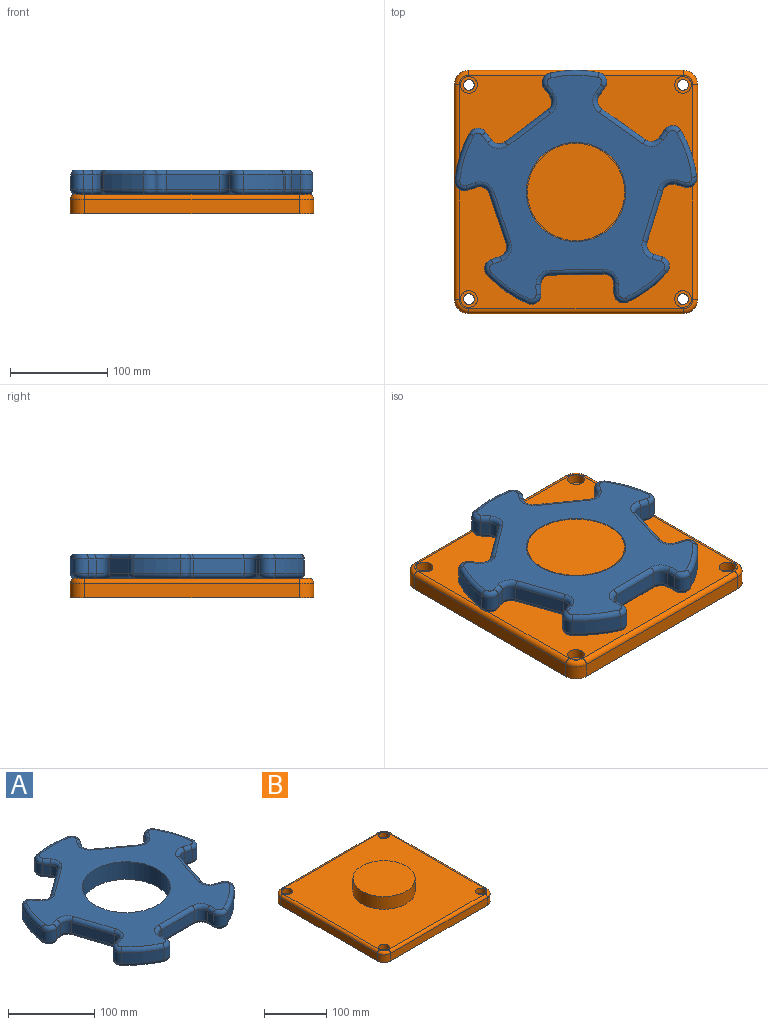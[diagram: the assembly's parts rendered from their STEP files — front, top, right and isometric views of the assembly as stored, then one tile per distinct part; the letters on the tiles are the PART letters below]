
ASSEMBLY  parts=2 mates=1
PART A: 123 faces, bbox 268.9x258.5x25 mm
  f0: plane 238.57x229.73mm, normal (0,0,1), area 21505.7mm2, adj f6,f83,f84,f85,f86,f87,f88,f89
  f1: plane 238.57x229.73mm, normal (0,0,-1), area 21505.7mm2, adj f6,f43,f44,f45,f46,f47,f48,f49
  f2: cylinder r=125mm len=47.82mm, axis (0,0,-1), area 759.5mm2, adj f34,f42,f74,f114
  f3: cylinder r=125mm len=50.29mm, axis (0,0,-1), area 759.5mm2, adj f27,f35,f75,f115
  f4: cylinder r=125mm len=47.82mm, axis (0,0,-1), area 759.5mm2, adj f20,f28,f59,f99
  f5: cylinder r=125mm len=40.68mm, axis (0,0,-1), area 759.5mm2, adj f13,f21,f43,f83
  f6: cylinder r=51mm len=102mm, axis (0,0,-1), area 8011.1mm2, adj f0,f1
  f7: cylinder r=125mm len=40.68mm, axis (0,0,-1), area 759.5mm2, adj f14,f41,f58,f98
  f8: plane 15x9.73mm, normal (-1,0,0), area 146mm2, adj f11,f14,f54,f94
  f9: plane 55x15mm, normal (0,-1,0), area 825mm2, adj f11,f12,f50,f90
  f10: plane 15x9.73mm, normal (1,0,0), area 146mm2, adj f12,f13,f46,f86
  f11: cylinder r=10mm len=15mm, axis (0,0,-1), area 235.6mm2, adj f8,f9,f52,f92
  f12: cylinder r=10mm len=15mm, axis (0,0,-1), area 235.6mm2, adj f9,f10,f48,f88
  f13: cylinder r=10mm len=15mm, axis (0,0,-1), area 299.5mm2, adj f5,f10,f44,f84
  f14: cylinder r=10mm len=15mm, axis (0,0,-1), area 299.5mm2, adj f7,f8,f56,f96
  f15: plane 15x9.26mm, normal (-0.31,0.95,0), area 146mm2, adj f18,f21,f47,f87
  f16: plane 52.31x17mm, normal (-0.95,-0.31,0), area 825mm2, adj f18,f19,f51,f91
  f17: plane 15x9.26mm, normal (0.31,-0.95,0), area 146mm2, adj f19,f20,f55,f95
  f18: cylinder r=10mm len=15mm, axis (0,0,-1), area 235.6mm2, adj f15,f16,f49,f89
  f19: cylinder r=10mm len=15mm, axis (0,0,-1), area 235.6mm2, adj f16,f17,f53,f93
  f20: cylinder r=10mm len=15mm, axis (0,0,-1), area 299.5mm2, adj f4,f17,f57,f97
  f21: cylinder r=10mm len=16.25mm, axis (0,0,-1), area 299.5mm2, adj f5,f15,f45,f85
  f22: plane 15x7.87mm, normal (0.81,0.59,0), area 146mm2, adj f25,f28,f63,f103
  f23: plane 44.5x32.33mm, normal (-0.59,0.81,0), area 825mm2, adj f25,f26,f67,f107
  f24: plane 15x7.87mm, normal (-0.81,-0.59,0), area 146mm2, adj f26,f27,f71,f111
  f25: cylinder r=10mm len=15mm, axis (0,0,-1), area 235.6mm2, adj f22,f23,f65,f105
  f26: cylinder r=10mm len=15mm, axis (0,0,-1), area 235.6mm2, adj f23,f24,f69,f109
  f27: cylinder r=10mm len=15.67mm, axis (0,0,-1), area 299.5mm2, adj f3,f24,f73,f113
  f28: cylinder r=10mm len=16.78mm, axis (0,0,-1), area 299.5mm2, adj f4,f22,f61,f101
  f29: plane 15x7.87mm, normal (0.81,-0.59,0), area 146mm2, adj f32,f35,f79,f119
  f30: plane 44.5x32.33mm, normal (0.59,0.81,0), area 825mm2, adj f32,f33,f82,f122
  f31: plane 15x7.87mm, normal (-0.81,0.59,0), area 146mm2, adj f33,f34,f78,f118
  f32: cylinder r=10mm len=15mm, axis (0,0,-1), area 235.6mm2, adj f29,f30,f81,f121
  f33: cylinder r=10mm len=15mm, axis (0,0,-1), area 235.6mm2, adj f30,f31,f80,f120
  f34: cylinder r=10mm len=16.78mm, axis (0,0,-1), area 299.5mm2, adj f2,f31,f76,f116
  f35: cylinder r=10mm len=15.67mm, axis (0,0,-1), area 299.5mm2, adj f3,f29,f77,f117
  f36: plane 15x9.26mm, normal (-0.31,-0.95,0), area 146mm2, adj f39,f42,f70,f110
  f37: plane 52.31x17mm, normal (0.95,-0.31,0), area 825mm2, adj f39,f40,f66,f106
  f38: plane 15x9.26mm, normal (0.31,0.95,0), area 146mm2, adj f40,f41,f62,f102
  f39: cylinder r=10mm len=15mm, axis (0,0,-1), area 235.6mm2, adj f36,f37,f68,f108
  f40: cylinder r=10mm len=15mm, axis (0,0,-1), area 235.6mm2, adj f37,f38,f64,f104
  f41: cylinder r=10mm len=16.25mm, axis (0,0,-1), area 299.5mm2, adj f7,f38,f60,f100
  f42: cylinder r=10mm len=15mm, axis (0,0,-1), area 299.5mm2, adj f2,f36,f72,f112
  f43: torus R=120mm, axis (0,0,1), area 391.9mm2, adj f1,f5,f44,f45
  f44: torus R=5mm, axis (0,0,1), area 128.3mm2, adj f1,f13,f43,f46
  f45: torus R=5mm, axis (0,0,1), area 128.3mm2, adj f1,f21,f43,f47
  f46: cylinder r=5mm len=9.73mm, axis (0,-1,0), area 76.4mm2, adj f1,f10,f44,f48
  f47: cylinder r=5mm len=10.8mm, axis (0.95,0.31,0), area 76.4mm2, adj f1,f15,f45,f49
  f48: torus R=15mm, axis (0,0,1), area 145.8mm2, adj f1,f12,f46,f50
  f49: torus R=15mm, axis (0,0,1), area 145.8mm2, adj f1,f18,f47,f51
  f50: cylinder r=5mm len=55mm, axis (-1,0,0), area 432mm2, adj f1,f9,f48,f52
  f51: cylinder r=5mm len=53.85mm, axis (-0.31,0.95,0), area 432mm2, adj f1,f16,f49,f53
  f52: torus R=15mm, axis (0,0,1), area 145.8mm2, adj f1,f11,f50,f54
  f53: torus R=15mm, axis (0,0,1), area 145.8mm2, adj f1,f19,f51,f55
  f54: cylinder r=5mm len=9.73mm, axis (0,1,0), area 76.4mm2, adj f1,f8,f52,f56
  f55: cylinder r=5mm len=10.8mm, axis (-0.95,-0.31,0), area 76.4mm2, adj f1,f17,f53,f57
  f56: torus R=5mm, axis (0,0,1), area 128.3mm2, adj f1,f14,f54,f58
  f57: torus R=5mm, axis (0,0,1), area 128.3mm2, adj f1,f20,f55,f59
  f58: torus R=120mm, axis (0,0,1), area 391.9mm2, adj f1,f7,f56,f60
  f59: torus R=120mm, axis (0,0,1), area 391.9mm2, adj f1,f4,f57,f61
  f60: torus R=5mm, axis (0,0,1), area 128.3mm2, adj f1,f41,f58,f62
  f61: torus R=5mm, axis (0,0,1), area 128.3mm2, adj f1,f28,f59,f63
  f62: cylinder r=5mm len=10.8mm, axis (0.95,-0.31,0), area 76.4mm2, adj f1,f38,f60,f64
  f63: cylinder r=5mm len=10.81mm, axis (0.59,-0.81,0), area 76.4mm2, adj f1,f22,f61,f65
  f64: torus R=15mm, axis (0,0,1), area 145.8mm2, adj f1,f40,f62,f66
  f65: torus R=15mm, axis (0,0,1), area 145.8mm2, adj f1,f25,f63,f67
  f66: cylinder r=5mm len=53.85mm, axis (-0.31,-0.95,0), area 432mm2, adj f1,f37,f64,f68
  f67: cylinder r=5mm len=47.44mm, axis (0.81,0.59,0), area 432mm2, adj f1,f23,f65,f69
  f68: torus R=15mm, axis (0,0,1), area 145.8mm2, adj f1,f39,f66,f70
  f69: torus R=15mm, axis (0,0,1), area 145.8mm2, adj f1,f26,f67,f71
  f70: cylinder r=5mm len=10.8mm, axis (-0.95,0.31,0), area 76.4mm2, adj f1,f36,f68,f72
  f71: cylinder r=5mm len=10.81mm, axis (-0.59,0.81,0), area 76.4mm2, adj f1,f24,f69,f73
  f72: torus R=5mm, axis (0,0,1), area 128.3mm2, adj f1,f42,f70,f74
  f73: torus R=5mm, axis (0,0,1), area 128.3mm2, adj f1,f27,f71,f75
  f74: torus R=120mm, axis (0,0,1), area 391.9mm2, adj f1,f2,f72,f76
  f75: torus R=120mm, axis (0,0,1), area 391.9mm2, adj f1,f3,f73,f77
  f76: torus R=5mm, axis (0,0,1), area 128.3mm2, adj f1,f34,f74,f78
  f77: torus R=5mm, axis (0,0,1), area 128.3mm2, adj f1,f35,f75,f79
  f78: cylinder r=5mm len=10.81mm, axis (0.59,0.81,0), area 76.4mm2, adj f1,f31,f76,f80
  f79: cylinder r=5mm len=10.81mm, axis (-0.59,-0.81,0), area 76.4mm2, adj f1,f29,f77,f81
  f80: torus R=15mm, axis (0,0,1), area 145.8mm2, adj f1,f33,f78,f82
  f81: torus R=15mm, axis (0,0,1), area 145.8mm2, adj f1,f32,f79,f82
  f82: cylinder r=5mm len=47.44mm, axis (0.81,-0.59,0), area 432mm2, adj f1,f30,f80,f81
  f83: torus R=120mm, axis (0,0,1), area 391.9mm2, adj f0,f5,f84,f85
  f84: torus R=5mm, axis (0,0,1), area 128.3mm2, adj f0,f13,f83,f86
  f85: torus R=5mm, axis (0,0,1), area 128.3mm2, adj f0,f21,f83,f87
  f86: cylinder r=5mm len=9.73mm, axis (0,1,0), area 76.4mm2, adj f0,f10,f84,f88
  f87: cylinder r=5mm len=10.8mm, axis (-0.95,-0.31,0), area 76.4mm2, adj f0,f15,f85,f89
  f88: torus R=15mm, axis (0,0,1), area 145.8mm2, adj f0,f12,f86,f90
  f89: torus R=15mm, axis (0,0,1), area 145.8mm2, adj f0,f18,f87,f91
  f90: cylinder r=5mm len=55mm, axis (1,0,0), area 432mm2, adj f0,f9,f88,f92
  f91: cylinder r=5mm len=53.85mm, axis (0.31,-0.95,0), area 432mm2, adj f0,f16,f89,f93
  f92: torus R=15mm, axis (0,0,1), area 145.8mm2, adj f0,f11,f90,f94
  f93: torus R=15mm, axis (0,0,1), area 145.8mm2, adj f0,f19,f91,f95
  f94: cylinder r=5mm len=9.73mm, axis (0,-1,0), area 76.4mm2, adj f0,f8,f92,f96
  f95: cylinder r=5mm len=10.8mm, axis (0.95,0.31,0), area 76.4mm2, adj f0,f17,f93,f97
  f96: torus R=5mm, axis (0,0,1), area 128.3mm2, adj f0,f14,f94,f98
  f97: torus R=5mm, axis (0,0,1), area 128.3mm2, adj f0,f20,f95,f99
  f98: torus R=120mm, axis (0,0,1), area 391.9mm2, adj f0,f7,f96,f100
  f99: torus R=120mm, axis (0,0,1), area 391.9mm2, adj f0,f4,f97,f101
  f100: torus R=5mm, axis (0,0,1), area 128.3mm2, adj f0,f41,f98,f102
  f101: torus R=5mm, axis (0,0,1), area 128.3mm2, adj f0,f28,f99,f103
  f102: cylinder r=5mm len=10.8mm, axis (-0.95,0.31,0), area 76.4mm2, adj f0,f38,f100,f104
  f103: cylinder r=5mm len=10.81mm, axis (-0.59,0.81,0), area 76.4mm2, adj f0,f22,f101,f105
  f104: torus R=15mm, axis (0,0,1), area 145.8mm2, adj f0,f40,f102,f106
  f105: torus R=15mm, axis (0,0,1), area 145.8mm2, adj f0,f25,f103,f107
  f106: cylinder r=5mm len=53.85mm, axis (0.31,0.95,0), area 432mm2, adj f0,f37,f104,f108
  f107: cylinder r=5mm len=47.44mm, axis (-0.81,-0.59,0), area 432mm2, adj f0,f23,f105,f109
  f108: torus R=15mm, axis (0,0,1), area 145.8mm2, adj f0,f39,f106,f110
  f109: torus R=15mm, axis (0,0,1), area 145.8mm2, adj f0,f26,f107,f111
  f110: cylinder r=5mm len=10.8mm, axis (0.95,-0.31,0), area 76.4mm2, adj f0,f36,f108,f112
  f111: cylinder r=5mm len=10.81mm, axis (0.59,-0.81,0), area 76.4mm2, adj f0,f24,f109,f113
  f112: torus R=5mm, axis (0,0,1), area 128.3mm2, adj f0,f42,f110,f114
  f113: torus R=5mm, axis (0,0,1), area 128.3mm2, adj f0,f27,f111,f115
  f114: torus R=120mm, axis (0,0,1), area 391.9mm2, adj f0,f2,f112,f116
  f115: torus R=120mm, axis (0,0,1), area 391.9mm2, adj f0,f3,f113,f117
  f116: torus R=5mm, axis (0,0,1), area 128.3mm2, adj f0,f34,f114,f118
  f117: torus R=5mm, axis (0,0,1), area 128.3mm2, adj f0,f35,f115,f119
  f118: cylinder r=5mm len=10.81mm, axis (-0.59,-0.81,0), area 76.4mm2, adj f0,f31,f116,f120
  f119: cylinder r=5mm len=10.81mm, axis (0.59,0.81,0), area 76.4mm2, adj f0,f29,f117,f121
  f120: torus R=15mm, axis (0,0,1), area 145.8mm2, adj f0,f33,f118,f122
  f121: torus R=15mm, axis (0,0,1), area 145.8mm2, adj f0,f32,f119,f122
  f122: cylinder r=5mm len=47.44mm, axis (-0.81,0.59,0), area 432mm2, adj f0,f30,f120,f121
PART B: 32 faces, bbox 252.5x252.5x45 mm
  f0: plane 220x15mm, normal (1,0,0), area 3300mm2, adj f5,f8,f11,f27
  f1: plane 220x15mm, normal (0,1,0), area 3300mm2, adj f5,f8,f9,f31
  f2: plane 220x15mm, normal (-1,0,0), area 3300mm2, adj f5,f9,f10,f28
  f3: plane 220x15mm, normal (0,-1,0), area 3300mm2, adj f5,f10,f11,f24
  f4: plane 240x240mm, normal (0,0,1), area 48725.4mm2, adj f6,f14,f17,f20,f23,f24,f25,f26
  f5: plane 250x250mm, normal (0,0,-1), area 61926.7mm2, adj f0,f1,f2,f3,f8,f9,f10,f11
  f6: cylinder r=50mm len=100mm, axis (0,0,-1), area 7854mm2, adj f4,f7
  f7: plane 100x100mm, normal (0,0,1), area 7854mm2, adj f6
  f8: cylinder r=15mm len=15mm, axis (0,0,-1), area 353.4mm2, adj f0,f1,f5,f29
  f9: cylinder r=15mm len=15mm, axis (0,0,1), area 353.4mm2, adj f1,f2,f5,f30
  f10: cylinder r=15mm len=15mm, axis (0,0,-1), area 353.4mm2, adj f2,f3,f5,f26
  f11: cylinder r=15mm len=15mm, axis (0,0,1), area 353.4mm2, adj f0,f3,f5,f25
  f12: cylinder r=5.5mm len=11mm, axis (0,0,1), area 345.6mm2, adj f5,f13
  f13: plane 17.25x17.25mm, normal (0,0,1), area 138.7mm2, adj f12,f14
  f14: cylinder r=8.62mm len=17.25mm, axis (0,0,1), area 541.9mm2, adj f4,f13
  f15: cylinder r=5.5mm len=11mm, axis (0,0,1), area 345.6mm2, adj f5,f16
  f16: plane 17.25x17.25mm, normal (0,0,1), area 138.7mm2, adj f15,f17
  f17: cylinder r=8.62mm len=17.25mm, axis (0,0,1), area 541.9mm2, adj f4,f16
  f18: cylinder r=5.5mm len=11mm, axis (0,0,1), area 345.6mm2, adj f5,f19
  f19: plane 17.25x17.25mm, normal (0,0,1), area 138.7mm2, adj f18,f20
  f20: cylinder r=8.62mm len=17.25mm, axis (0,0,1), area 541.9mm2, adj f4,f19
  f21: cylinder r=5.5mm len=11mm, axis (0,0,1), area 345.6mm2, adj f5,f22
  f22: plane 17.25x17.25mm, normal (0,0,1), area 138.7mm2, adj f21,f23
  f23: cylinder r=8.62mm len=17.25mm, axis (0,0,1), area 541.9mm2, adj f4,f22
  f24: cylinder r=5mm len=220mm, axis (-1,0,0), area 1727.9mm2, adj f3,f4,f25,f26
  f25: torus R=10mm, axis (0,0,1), area 162.6mm2, adj f4,f11,f24,f27
  f26: torus R=10mm, axis (0,0,1), area 162.6mm2, adj f4,f10,f24,f28
  f27: cylinder r=5mm len=220mm, axis (0,-1,0), area 1727.9mm2, adj f0,f4,f25,f29
  f28: cylinder r=5mm len=220mm, axis (0,1,0), area 1727.9mm2, adj f2,f4,f26,f30
  f29: torus R=10mm, axis (0,0,1), area 162.6mm2, adj f4,f8,f27,f31
  f30: torus R=10mm, axis (0,0,1), area 162.6mm2, adj f4,f9,f28,f31
  f31: cylinder r=5mm len=220mm, axis (1,0,0), area 1727.9mm2, adj f1,f4,f29,f30
PLACE A rot(axis=(0,0,1),0.8deg) t=(0,0,0)mm
PLACE B at identity fixed
MATE revolute B.f6 <-> A.f2  axis (0,0,1) through (0,0,45)mm
